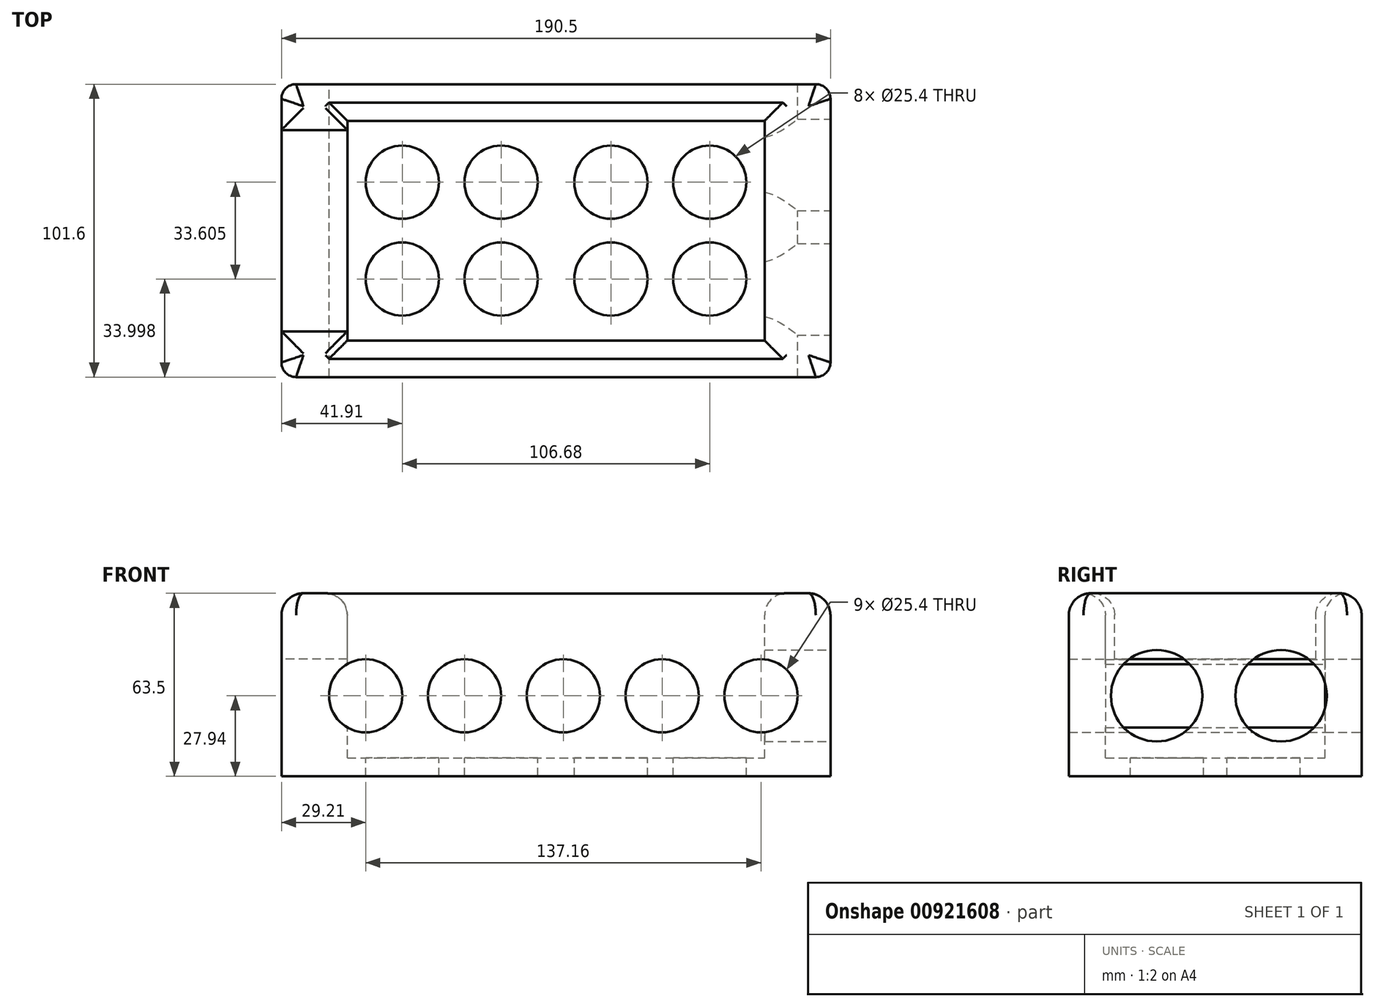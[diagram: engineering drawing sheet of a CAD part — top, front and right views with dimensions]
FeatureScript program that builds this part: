
annotation { "Feature Type Name" : "Feature", "Feature Type Description" : "" }
export const myFeature = defineFeature(function(context is Context, id is Id, definition is map)
    precondition{}
    {
        {
            var Q0;
            Q0=qCreatedBy(makeId("Top.planeOp"),FACE);
            var sketch = newSketch(context, id + "F0", { "sketchPlane" : qUnion([Q0])});
            skLineSegment(sketch, "E0.bottom", {"start": v(95.25, 50.8) * mm, "end": v(-95.25, 50.8) * mm});
            skLineSegment(sketch, "E0.top", {"start": v(95.25, -50.8) * mm, "end": v(-95.25, -50.8) * mm});
            skLineSegment(sketch, "E0.left", {"start": v(95.25, 50.8) * mm, "end": v(95.25, -50.8) * mm});
            skLineSegment(sketch, "E0.right", {"start": v(-95.25, 50.8) * mm, "end": v(-95.25, -50.8) * mm});
            skPoint(sketch, "E0.middle", {"position": v(0, 0) * mm});
            skSolve(sketch);
        }
        {
            var Q0;
            Q0 = qSketchRegion(id + "F0", true);
            extrude(context, id + "F1", {"entities" : qUnion([Q0]), "oppositeDirection" : true, "depth" : 63.5 * mm, "offsetDistance" : 25.4 * mm});
        }
        {
            var Q0;
            Q0=makeQuery(id+"F1.opExtrude","CAP_FACE",FACE,{"disambiguationData":[OSD([sQuery(id+"F0.wireOp",EDGE,"E0.bottom"),sQuery(id+"F0.wireOp",EDGE,"E0.top"),sQuery(id+"F0.wireOp",EDGE,"E0.left"),sQuery(id+"F0.wireOp",EDGE,"E0.right")])],"isStart":true});
            var sketch = newSketch(context, id + "F2", { "sketchPlane" : qUnion([Q0])});
            skLineSegment(sketch, "E1.bottom", {"start": v(72.4, 38.1) * mm, "end": v(-72.4, 38.1) * mm});
            skLineSegment(sketch, "E1.top", {"start": v(72.4, -38.1) * mm, "end": v(-72.4, -38.1) * mm});
            skLineSegment(sketch, "E1.left", {"start": v(72.4, 38.1) * mm, "end": v(72.4, -38.1) * mm});
            skLineSegment(sketch, "E1.right", {"start": v(-72.4, 38.1) * mm, "end": v(-72.4, -38.1) * mm});
            skPoint(sketch, "E1.middle", {"position": v(0, 0) * mm});
            skSolve(sketch);
        }
        {
            var Q0;
            Q0 = qSketchRegion(id + "F2", true);
            extrude(context, id + "F3", {"entities" : qUnion([Q0]), "operationType" : NewBodyOperationType.REMOVE, "endBound" : BoundingType.UP_TO_NEXT, "oppositeDirection" : true, "depth" : 25.4 * mm, "hasOffset" : true, "offsetDistance" : 6.35 * mm});
        }
        {
            var Q0;
            Q0=makeQuery(id+"F1.opExtrude","SWEPT_EDGE",EDGE,{"disambiguationData":[OSD([sQuery(id+"F0.wireOp",EDGE,"E0.top"),sQuery(id+"F0.wireOp",EDGE,"E0.right")])]});
            var Q1;
            Q1=makeQuery(id+"F1.opExtrude","SWEPT_EDGE",EDGE,{"disambiguationData":[OSD([sQuery(id+"F0.wireOp",EDGE,"E0.bottom"),sQuery(id+"F0.wireOp",EDGE,"E0.left")])]});
            var Q2;
            Q2=makeQuery(id+"F1.opExtrude","SWEPT_EDGE",EDGE,{"disambiguationData":[OSD([sQuery(id+"F0.wireOp",EDGE,"E0.top"),sQuery(id+"F0.wireOp",EDGE,"E0.left")])]});
            var Q3;
            Q3=makeQuery(id+"F1.opExtrude","SWEPT_EDGE",EDGE,{"disambiguationData":[OSD([sQuery(id+"F0.wireOp",EDGE,"E0.bottom"),sQuery(id+"F0.wireOp",EDGE,"E0.right")])]});
            fillet(context, id + "F4", {"entities" : qUnion([Q0, Q1, Q2, Q3]), "radius" : 5.08 * mm, "tangentPropagation" : true, "allowEdgeOverflow" : false});
        }
        {
            var Q0;
            Q0=makeQuery(id+"F1.opExtrude","SWEPT_FACE",FACE,{"disambiguationData":[OSD([sQuery(id+"F0.wireOp",EDGE,"E0.right")])]});
            var sketch = newSketch(context, id + "F5", { "sketchPlane" : qUnion([Q0])});
            skLineSegment(sketch, "E2.bottom", {"start": v(-34.92, 2.54) * mm, "end": v(34.93, 2.54) * mm});
            skLineSegment(sketch, "E2.top", {"start": v(-34.92, -22.86) * mm, "end": v(34.93, -22.86) * mm});
            skLineSegment(sketch, "E2.left", {"start": v(-34.92, 2.54) * mm, "end": v(-34.92, -22.86) * mm});
            skLineSegment(sketch, "E2.right", {"start": v(34.93, 2.54) * mm, "end": v(34.93, -22.86) * mm});
            skLineSegment(sketch, "E3", {"start": v(0, -7.62) * mm, "end": v(0, -63.5) * mm, "construction": true});
            skSolve(sketch);
        }
        {
            var Q0;
            Q0 = qSketchRegion(id + "F5", true);
            extrude(context, id + "F6", {"entities" : qUnion([Q0]), "operationType" : NewBodyOperationType.REMOVE, "endBound" : BoundingType.UP_TO_NEXT, "oppositeDirection" : true, "depth" : 25.4 * mm, "offsetDistance" : 25.4 * mm});
        }
        {
            var Q0;
            Q0=makeQuery(id+"F1.opExtrude","CAP_FACE",FACE,{"disambiguationData":[OSD([sQuery(id+"F0.wireOp",EDGE,"E0.bottom"),sQuery(id+"F0.wireOp",EDGE,"E0.top"),sQuery(id+"F0.wireOp",EDGE,"E0.left"),sQuery(id+"F0.wireOp",EDGE,"E0.right")])],"isStart":false});
            cPlane(context, id + "F7", {"entities" : qUnion([Q0]), "cplaneType" : CPlaneType.OFFSET, "offset" : 6.35 * mm, "oppositeDirection" : true, "width" : 152.4 * mm, "height" : 152.4 * mm});
        }
        {
            var Q0;
            Q0=qCreatedBy(id+"F7.planeOp",FACE);
            var sketch = newSketch(context, id + "F8", { "sketchPlane" : qUnion([Q0])});
            skLineSegment(sketch, "E4.bottom", {"start": v(-77.47, -43.18) * mm, "end": v(77.47, -43.18) * mm});
            skLineSegment(sketch, "E4.top", {"start": v(-77.47, 43.18) * mm, "end": v(77.47, 43.18) * mm});
            skLineSegment(sketch, "E4.left", {"start": v(-77.47, 43.18) * mm, "end": v(-77.47, -43.18) * mm});
            skLineSegment(sketch, "E4.right", {"start": v(77.47, -43.18) * mm, "end": v(77.47, 43.18) * mm});
            skPoint(sketch, "E4.middle", {"position": v(0, 0) * mm});
            skLineSegment(sketch, "E5.bottom", {"start": v(-114.3, 63.5) * mm, "end": v(114.3, 63.5) * mm});
            skLineSegment(sketch, "E5.top", {"start": v(-114.3, -63.5) * mm, "end": v(114.3, -63.5) * mm});
            skLineSegment(sketch, "E5.left", {"start": v(-114.3, 63.5) * mm, "end": v(-114.3, -63.5) * mm});
            skLineSegment(sketch, "E5.right", {"start": v(114.3, 63.5) * mm, "end": v(114.3, -63.5) * mm});
            skSolve(sketch);
        }
        {
            var Q0;
            Q0=makeQuery(id+"F1.opExtrude","CAP_FACE",FACE,{"disambiguationData":[OSD([sQuery(id+"F0.wireOp",EDGE,"E0.bottom"),sQuery(id+"F0.wireOp",EDGE,"E0.top"),sQuery(id+"F0.wireOp",EDGE,"E0.left"),sQuery(id+"F0.wireOp",EDGE,"E0.right")])],"isStart":true});
            fillet(context, id + "F9", {"entities" : qUnion([Q0]), "radius" : 7.62 * mm, "tangentPropagation" : true, "allowEdgeOverflow" : false});
        }
        {
            var Q0;
            Q0=qCreatedBy(makeId("Front.planeOp"),FACE);
            var sketch = newSketch(context, id + "F10", { "sketchPlane" : qUnion([Q0])});
            skCircle(sketch, "E6", {"center": v(71.12, -35.56) * mm, "radius": 12.7 * mm});
            skCircle(sketch, "E7.1.0.0", {"center": v(36.83, -35.56) * mm, "radius": 12.7 * mm});
            skCircle(sketch, "E7.2.0.0", {"center": v(2.54, -35.56) * mm, "radius": 12.7 * mm});
            skCircle(sketch, "E7.3.0.0", {"center": v(-31.75, -35.56) * mm, "radius": 12.7 * mm});
            skCircle(sketch, "E7.4.0.0", {"center": v(-66.04, -35.56) * mm, "radius": 12.7 * mm});
            skLineSegment(sketch, "E7.direction1", {"start": v(71.12, -35.56) * mm, "end": v(36.83, -35.56) * mm, "construction": true});
            skSolve(sketch);
        }
        {
            var Q0;
            Q0 = qSketchRegion(id + "F10", true);
            extrude(context, id + "F11", {"entities" : qUnion([Q0]), "operationType" : NewBodyOperationType.REMOVE, "endBound" : BoundingType.THROUGH_ALL, "depth" : 25.4 * mm, "offsetDistance" : 25.4 * mm, "hasSecondDirection" : true, "secondDirectionBound" : SecondDirectionBoundingType.THROUGH_ALL, "secondDirectionOppositeDirection" : true, "secondDirectionDepth" : 25.4 * mm});
        }
        {
            var Q0;
            Q0=makeQuery(id+"F1.opExtrude","SWEPT_FACE",FACE,{"disambiguationData":[OSD([sQuery(id+"F0.wireOp",EDGE,"E0.left")])]});
            var sketch = newSketch(context, id + "F12", { "sketchPlane" : qUnion([Q0])});
            skCircle(sketch, "E8", {"center": v(-20.32, -35.56) * mm, "radius": 15.88 * mm});
            skPoint(sketch, "E8.centerSnap0", {"position": v(-45.72, -35.56) * mm});
            skCircle(sketch, "E9.1.0.0", {"center": v(22.86, -35.56) * mm, "radius": 15.88 * mm});
            skLineSegment(sketch, "E9.direction1", {"start": v(-20.32, -35.56) * mm, "end": v(22.86, -35.56) * mm, "construction": true});
            skSolve(sketch);
        }
        {
            var Q0;
            Q0 = qSketchRegion(id + "F12", true);
            extrude(context, id + "F13", {"entities" : qUnion([Q0]), "operationType" : NewBodyOperationType.REMOVE, "endBound" : BoundingType.UP_TO_NEXT, "oppositeDirection" : true, "depth" : 25.4 * mm, "offsetDistance" : 25.4 * mm});
        }
        {
            var Q0;
            Q0=makeQuery(id+"F3.boolean.opBoolean","COPY",FACE,{"derivedFrom":makeQuery(id+"F3.opExtrude","CAP_FACE",FACE,{"disambiguationData":[OSD([sQuery(id+"F2.wireOp",EDGE,"E1.bottom"),sQuery(id+"F2.wireOp",EDGE,"E1.top"),sQuery(id+"F2.wireOp",EDGE,"E1.left"),sQuery(id+"F2.wireOp",EDGE,"E1.right")])],"isStart":false})});
            var sketch = newSketch(context, id + "F14", { "sketchPlane" : qUnion([Q0])});
            skCircle(sketch, "E10", {"center": v(53.34, 16.8) * mm, "radius": 12.7 * mm});
            skCircle(sketch, "E11.1.0.0", {"center": v(19.05, 16.8) * mm, "radius": 12.7 * mm});
            skLineSegment(sketch, "E11.direction1", {"start": v(53.34, 16.8) * mm, "end": v(19.05, 16.8) * mm, "construction": true});
            skLineSegment(sketch, "E11.direction2", {"start": v(53.34, 16.8) * mm, "end": v(53.34, -20.79) * mm, "construction": true});
            skCircle(sketch, "E12.MirrorC", {"center": v(-53.34, 16.8) * mm, "radius": 12.7 * mm});
            skCircle(sketch, "E13.MirrorC", {"center": v(-19.05, 16.8) * mm, "radius": 12.7 * mm});
            skCircle(sketch, "E14.MirrorC", {"center": v(-53.34, -16.8) * mm, "radius": 12.7 * mm});
            skCircle(sketch, "E15.MirrorC", {"center": v(-19.05, -16.8) * mm, "radius": 12.7 * mm});
            skCircle(sketch, "E16.MirrorC", {"center": v(53.34, -16.8) * mm, "radius": 12.7 * mm});
            skCircle(sketch, "E17.MirrorC", {"center": v(19.05, -16.8) * mm, "radius": 12.7 * mm});
            skSolve(sketch);
        }
        {
            var Q0;
            Q0 = qSketchRegion(id + "F14", true);
            extrude(context, id + "F15", {"entities" : qUnion([Q0]), "operationType" : NewBodyOperationType.REMOVE, "endBound" : BoundingType.THROUGH_ALL, "oppositeDirection" : true, "depth" : 25.4 * mm, "offsetDistance" : 25.4 * mm});
        }
    });
